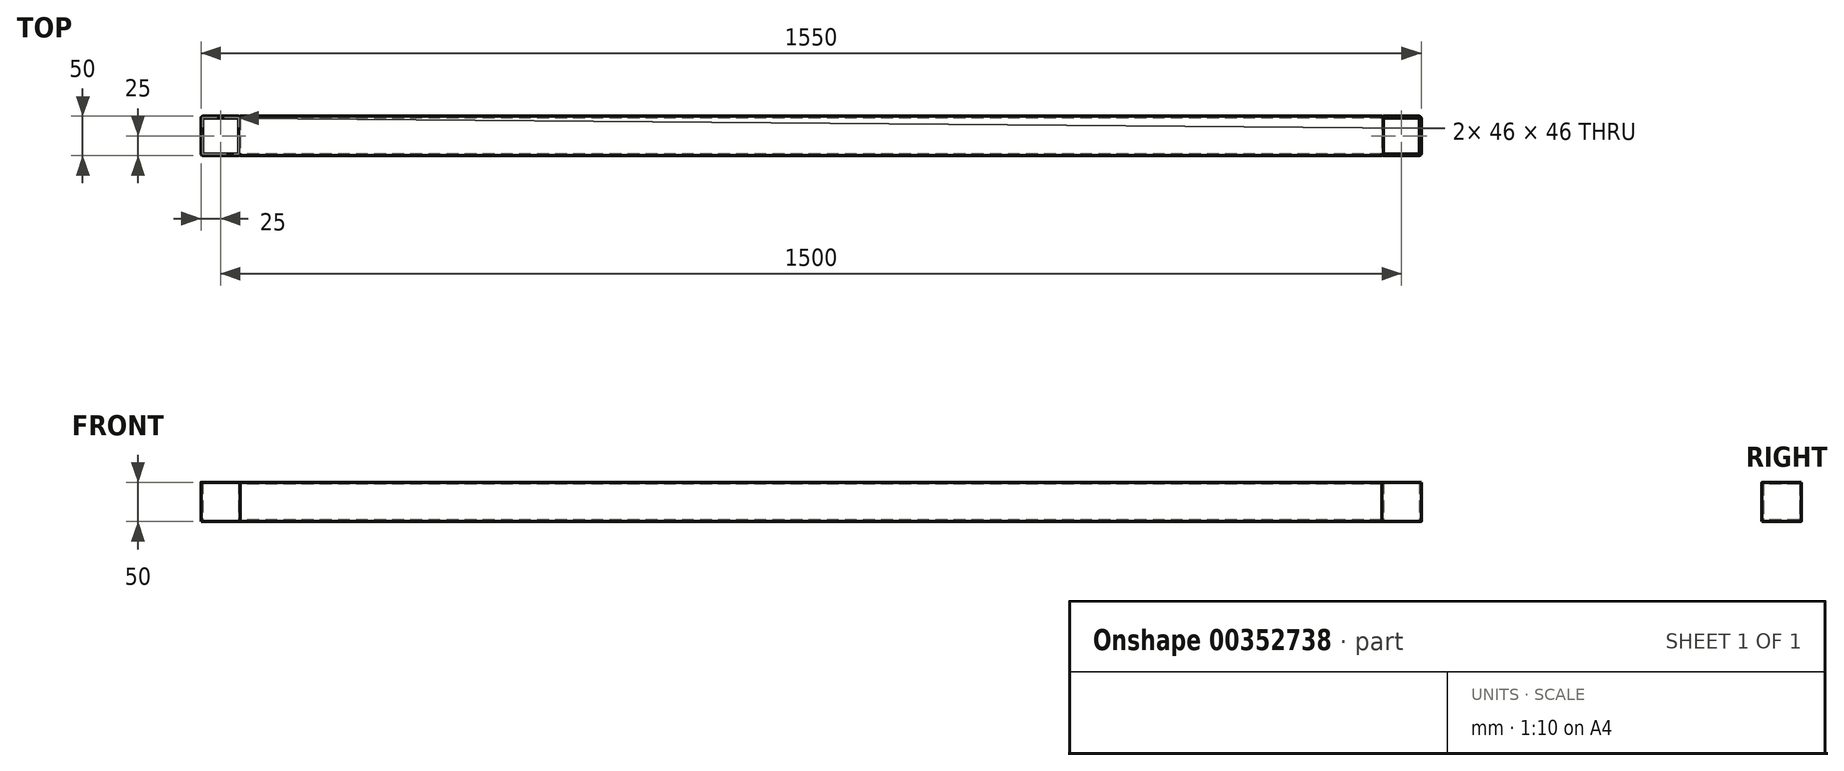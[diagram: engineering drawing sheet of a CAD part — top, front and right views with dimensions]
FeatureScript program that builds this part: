
annotation { "Feature Type Name" : "Feature", "Feature Type Description" : "" }
export const myFeature = defineFeature(function(context is Context, id is Id, definition is map)
    precondition{}
    {
        {
            var Q0;
            Q0=qCreatedBy(makeId("Right.planeOp"),FACE);
            var sketch = newSketch(context, id + "F0", { "sketchPlane" : qUnion([Q0])});
            skLineSegment(sketch, "E0.bottom", {"start": v(-177.54, 425) * mm, "end": v(-222.46, 425) * mm});
            skLineSegment(sketch, "E0.top", {"start": v(-177.54, 375) * mm, "end": v(-222.46, 375) * mm});
            skLineSegment(sketch, "E0.left", {"start": v(-175, 422.46) * mm, "end": v(-175, 377.54) * mm});
            skLineSegment(sketch, "E0.right", {"start": v(-225, 422.46) * mm, "end": v(-225, 377.54) * mm});
            skPoint(sketch, "E0.middle", {"position": v(-200, 400) * mm});
            skPoint(sketch, "E1.visualSharp", {"position": v(-225, 425) * mm});
            skArc(sketch, "E1.filletArc", {"start": v(-222.46, 425) * mm, "mid": v(-224.26, 424.26) * mm, "end": v(-225, 422.46) * mm});
            skPoint(sketch, "E2.visualSharp", {"position": v(-175, 425) * mm});
            skArc(sketch, "E2.filletArc", {"start": v(-175, 422.46) * mm, "mid": v(-175.74, 424.26) * mm, "end": v(-177.54, 425) * mm});
            skPoint(sketch, "E3.visualSharp", {"position": v(-175, 375) * mm});
            skArc(sketch, "E3.filletArc", {"start": v(-177.54, 375) * mm, "mid": v(-175.74, 375.74) * mm, "end": v(-175, 377.54) * mm});
            skPoint(sketch, "E4.visualSharp", {"position": v(-225, 375) * mm});
            skArc(sketch, "E4.filletArc", {"start": v(-225, 377.54) * mm, "mid": v(-224.26, 375.74) * mm, "end": v(-222.46, 375) * mm});
            skLineSegment(sketch, "E5.0", {"start": v(-177, 423) * mm, "end": v(-223, 423) * mm});
            skLineSegment(sketch, "E5.1", {"start": v(-177, 423) * mm, "end": v(-177, 377) * mm});
            skLineSegment(sketch, "E5.2", {"start": v(-177, 377) * mm, "end": v(-223, 377) * mm});
            skLineSegment(sketch, "E5.3", {"start": v(-223, 423) * mm, "end": v(-223, 377) * mm});
            skSolve(sketch);
        }
        {
            var Q0;
            Q0=qSketchRegion(id+"F0",true);
            extrude(context, id + "F1", {"entities" : qUnion([Q0]), "endBound" : BoundingType.SYMMETRIC, "depth" : 1450 * mm});
        }
        {
            var Q0;
            Q0=qCreatedBy(makeId("Top.planeOp"),FACE);
            cPlane(context, id + "F2", {"entities" : qUnion([Q0]), "cplaneType" : CPlaneType.OFFSET, "offset" : 400 * mm, "width" : 152.4 * mm, "height" : 152.4 * mm});
        }
        {
            var Q0;
            Q0=qCreatedBy(id+"F2.planeOp",FACE);
            var sketch = newSketch(context, id + "F3", { "sketchPlane" : qUnion([Q0])});
            skLineSegment(sketch, "E6.bottom", {"start": v(772.46, -225) * mm, "end": v(727.54, -225) * mm});
            skLineSegment(sketch, "E6.top", {"start": v(772.46, -175) * mm, "end": v(727.54, -175) * mm});
            skLineSegment(sketch, "E6.left", {"start": v(775, -222.46) * mm, "end": v(775, -177.54) * mm});
            skLineSegment(sketch, "E6.right", {"start": v(725, -222.46) * mm, "end": v(725, -177.54) * mm});
            skPoint(sketch, "E6.middle", {"position": v(750, -200) * mm});
            skPoint(sketch, "E7.visualSharp", {"position": v(725, -175) * mm});
            skArc(sketch, "E7.filletArc", {"start": v(727.54, -175) * mm, "mid": v(725.74, -175.74) * mm, "end": v(725, -177.54) * mm});
            skPoint(sketch, "E8.visualSharp", {"position": v(775, -175) * mm});
            skArc(sketch, "E8.filletArc", {"start": v(775, -177.54) * mm, "mid": v(774.26, -175.74) * mm, "end": v(772.46, -175) * mm});
            skPoint(sketch, "E9.visualSharp", {"position": v(775, -225) * mm});
            skArc(sketch, "E9.filletArc", {"start": v(772.46, -225) * mm, "mid": v(774.26, -224.26) * mm, "end": v(775, -222.46) * mm});
            skPoint(sketch, "E10.visualSharp", {"position": v(725, -225) * mm});
            skArc(sketch, "E10.filletArc", {"start": v(725, -222.46) * mm, "mid": v(725.74, -224.26) * mm, "end": v(727.54, -225) * mm});
            skLineSegment(sketch, "E11.0", {"start": v(773, -223) * mm, "end": v(727, -223) * mm});
            skLineSegment(sketch, "E11.1", {"start": v(773, -223) * mm, "end": v(773, -177) * mm});
            skLineSegment(sketch, "E11.2", {"start": v(773, -177) * mm, "end": v(727, -177) * mm});
            skLineSegment(sketch, "E11.3", {"start": v(727, -223) * mm, "end": v(727, -177) * mm});
            skArc(sketch, "E12.MirrorCS", {"start": v(-772.46, -225) * mm, "mid": v(-774.26, -224.26) * mm, "end": v(-775, -222.46) * mm});
            skArc(sketch, "E13.MirrorCS", {"start": v(-727.54, -175) * mm, "mid": v(-725.74, -175.74) * mm, "end": v(-725, -177.54) * mm});
            skArc(sketch, "E14.MirrorCS", {"start": v(-775, -177.54) * mm, "mid": v(-774.26, -175.74) * mm, "end": v(-772.46, -175) * mm});
            skLineSegment(sketch, "E15.MirrorCS", {"start": v(-775, -222.46) * mm, "end": v(-775, -177.54) * mm});
            skPoint(sketch, "E16.MirrorP", {"position": v(-775, -225) * mm});
            skLineSegment(sketch, "E17.MirrorCS", {"start": v(-773, -223) * mm, "end": v(-773, -177) * mm});
            skPoint(sketch, "E18.MirrorP", {"position": v(-750, -200) * mm});
            skLineSegment(sketch, "E19.MirrorCS", {"start": v(-772.46, -225) * mm, "end": v(-727.54, -225) * mm});
            skPoint(sketch, "E20.MirrorP", {"position": v(-725, -175) * mm});
            skLineSegment(sketch, "E21.MirrorCS", {"start": v(-773, -177) * mm, "end": v(-727, -177) * mm});
            skLineSegment(sketch, "E22.MirrorCS", {"start": v(-773, -223) * mm, "end": v(-727, -223) * mm});
            skArc(sketch, "E23.MirrorCS", {"start": v(-725, -222.46) * mm, "mid": v(-725.74, -224.26) * mm, "end": v(-727.54, -225) * mm});
            skPoint(sketch, "E24.MirrorP", {"position": v(-775, -175) * mm});
            skLineSegment(sketch, "E25.MirrorCS", {"start": v(-727, -223) * mm, "end": v(-727, -177) * mm});
            skLineSegment(sketch, "E26.MirrorCS", {"start": v(-772.46, -175) * mm, "end": v(-727.54, -175) * mm});
            skLineSegment(sketch, "E27.MirrorCS", {"start": v(-725, -222.46) * mm, "end": v(-725, -177.54) * mm});
            skSolve(sketch);
        }
        {
            var Q0;
            Q0=qSketchRegion(id+"F3",true);
            extrude(context, id + "F4", {"entities" : qUnion([Q0]), "operationType" : NewBodyOperationType.ADD, "endBound" : BoundingType.SYMMETRIC, "depth" : 50 * mm});
        }
    });
